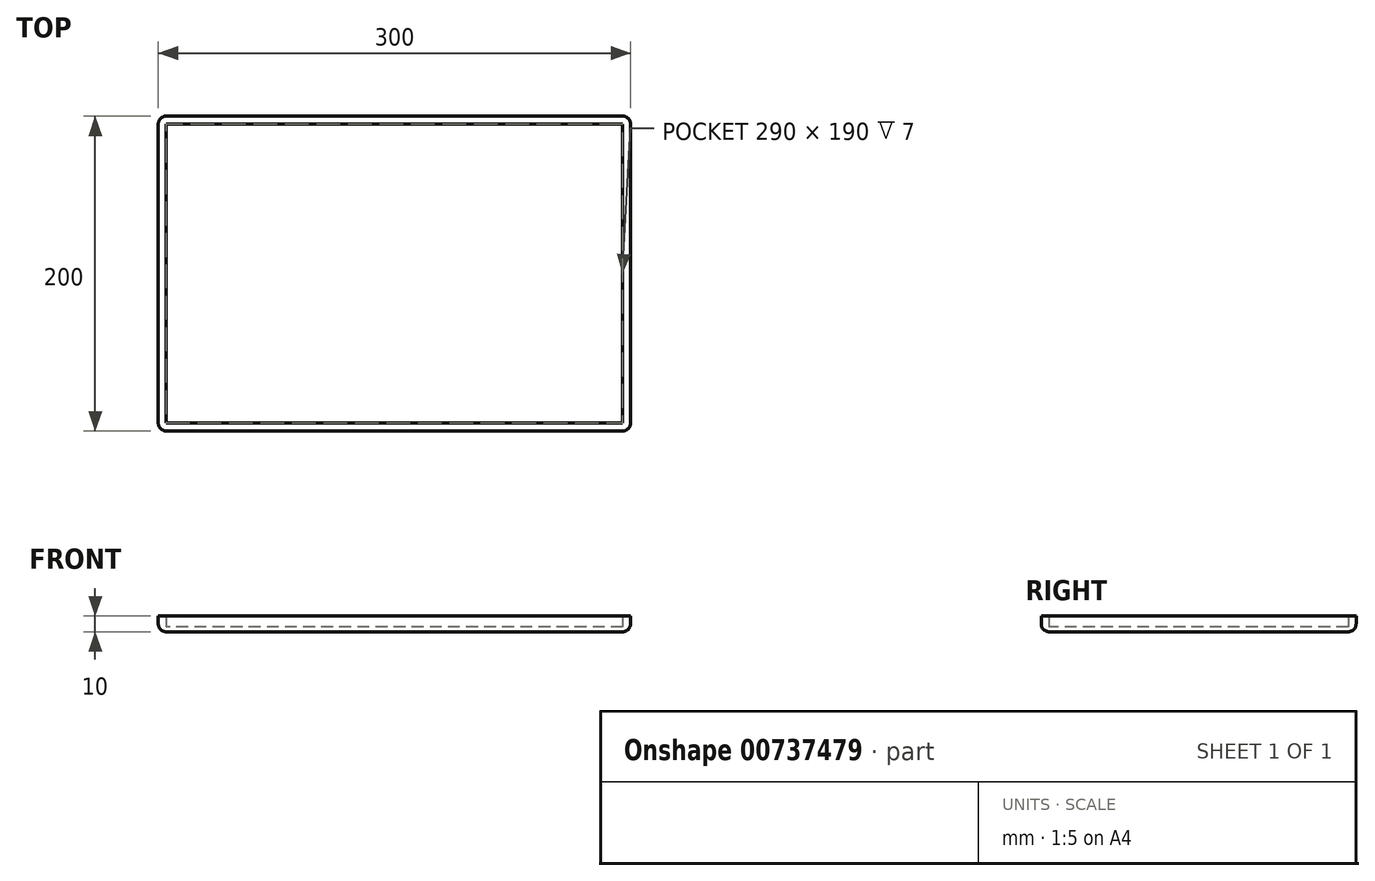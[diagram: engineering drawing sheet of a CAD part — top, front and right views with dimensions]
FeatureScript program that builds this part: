
annotation { "Feature Type Name" : "Feature", "Feature Type Description" : "" }
export const myFeature = defineFeature(function(context is Context, id is Id, definition is map)
    precondition{}
    {
        {
            var Q0;
            Q0=qCreatedBy(makeId("Top.planeOp"),FACE);
            var sketch = newSketch(context, id + "F0", { "sketchPlane" : qUnion([Q0])});
            skLineSegment(sketch, "E0.bottom", {"start": v(150, 100) * mm, "end": v(-150, 100) * mm});
            skLineSegment(sketch, "E0.top", {"start": v(150, -100) * mm, "end": v(-150, -100) * mm});
            skLineSegment(sketch, "E0.left", {"start": v(150, 100) * mm, "end": v(150, -100) * mm});
            skLineSegment(sketch, "E0.right", {"start": v(-150, 100) * mm, "end": v(-150, -100) * mm});
            skPoint(sketch, "E0.middle", {"position": v(0, 0) * mm});
            skLineSegment(sketch, "E1.bottom", {"start": v(145, 95) * mm, "end": v(-145, 95) * mm});
            skLineSegment(sketch, "E1.top", {"start": v(145, -95) * mm, "end": v(-145, -95) * mm});
            skLineSegment(sketch, "E1.left", {"start": v(145, 95) * mm, "end": v(145, -95) * mm});
            skLineSegment(sketch, "E1.right", {"start": v(-145, 95) * mm, "end": v(-145, -95) * mm});
            skLineSegment(sketch, "E2.bottom", {"start": v(147.5, 97.5) * mm, "end": v(-147.5, 97.5) * mm});
            skLineSegment(sketch, "E2.top", {"start": v(147.5, -97.5) * mm, "end": v(-147.5, -97.5) * mm});
            skLineSegment(sketch, "E2.left", {"start": v(147.5, 97.5) * mm, "end": v(147.5, -97.5) * mm});
            skLineSegment(sketch, "E2.right", {"start": v(-147.5, 97.5) * mm, "end": v(-147.5, -97.5) * mm});
            skSolve(sketch);
        }
        {
            var Q0;
            Q0=makeQuery(id+"F0.imprint","IMPRINT",FACE,{"disambiguationData":[TD([[makeQuery(id+"F0.imprint","IMPRINT",EDGE,{"derivedFrom":sQuery(id+"F0.wireOp",EDGE,"E0.bottom")}),1.0]])]});
            var Q1;
            Q1=makeQuery(id+"F0.imprint","IMPRINT",FACE,{"disambiguationData":[TD([[makeQuery(id+"F0.imprint","IMPRINT",EDGE,{"derivedFrom":sQuery(id+"F0.wireOp",EDGE,"E1.bottom")}),-1.0]])]});
            extrude(context, id + "F1", {"entities" : qUnion([Q0, Q1]), "depth" : 10 * mm, "offsetDistance" : 25 * mm});
        }
        {
            var Q0;
            Q0=makeQuery(id+"F0.imprint","IMPRINT",FACE,{"disambiguationData":[TD([[makeQuery(id+"F0.imprint","IMPRINT",EDGE,{"derivedFrom":sQuery(id+"F0.wireOp",EDGE,"E1.bottom")}),-1.0]])]});
            extrude(context, id + "F2", {"entities" : qUnion([Q0]), "operationType" : NewBodyOperationType.REMOVE, "depth" : 3 * mm, "offsetDistance" : 25 * mm});
        }
        {
            var Q0;
            Q0=makeQuery(id+"F0.imprint","IMPRINT",FACE,{"disambiguationData":[TD([[makeQuery(id+"F0.imprint","IMPRINT",EDGE,{"derivedFrom":sQuery(id+"F0.wireOp",EDGE,"E1.bottom")}),-1.0]])]});
            var Q1;
            Q1=makeQuery(id+"F0.imprint","IMPRINT",FACE,{"disambiguationData":[TD([[makeQuery(id+"F0.imprint","IMPRINT",EDGE,{"derivedFrom":sQuery(id+"F0.wireOp",EDGE,"E1.bottom")}),1.0]])]});
            extrude(context, id + "F3", {"entities" : qUnion([Q0, Q1]), "operationType" : NewBodyOperationType.ADD, "depth" : 3 * mm, "offsetDistance" : 25 * mm});
        }
        {
            var Q0;
            Q0=makeQuery(id+"F1.opExtrude","SWEPT_EDGE",EDGE,{"disambiguationData":[OSD([sQuery(id+"F0.wireOp",EDGE,"E0.top"),sQuery(id+"F0.wireOp",EDGE,"E0.right")])]});
            var Q1;
            Q1=makeQuery(id+"F1.opExtrude","SWEPT_EDGE",EDGE,{"disambiguationData":[OSD([sQuery(id+"F0.wireOp",EDGE,"E0.top"),sQuery(id+"F0.wireOp",EDGE,"E0.left")])]});
            var Q2;
            Q2=makeQuery(id+"F1.opExtrude","SWEPT_EDGE",EDGE,{"disambiguationData":[OSD([sQuery(id+"F0.wireOp",EDGE,"E0.bottom"),sQuery(id+"F0.wireOp",EDGE,"E0.left")])]});
            var Q3;
            Q3=makeQuery(id+"F1.opExtrude","SWEPT_EDGE",EDGE,{"disambiguationData":[OSD([sQuery(id+"F0.wireOp",EDGE,"E0.bottom"),sQuery(id+"F0.wireOp",EDGE,"E0.right")])]});
            fillet(context, id + "F4", {"entities" : qUnion([Q0, Q1, Q2, Q3]), "radius" : 5 * mm, "tangentPropagation" : true, "allowEdgeOverflow" : false});
        }
        {
            var Q0;
            Q0=makeQuery(id+"F3.boolean.opBoolean","MERGE",FACE,{"derivedFrom":[makeQuery(id+"F1.opExtrude","CAP_FACE",FACE,{"disambiguationData":[OSD([sQuery(id+"F0.wireOp",EDGE,"E0.bottom"),sQuery(id+"F0.wireOp",EDGE,"E0.top"),sQuery(id+"F0.wireOp",EDGE,"E0.left"),sQuery(id+"F0.wireOp",EDGE,"E0.right"),sQuery(id+"F0.wireOp",EDGE,"E1.bottom"),sQuery(id+"F0.wireOp",EDGE,"E1.top"),sQuery(id+"F0.wireOp",EDGE,"E1.left"),sQuery(id+"F0.wireOp",EDGE,"E1.right")])],"isStart":true}),makeQuery(id+"F3.opExtrude","CAP_FACE",FACE,{"disambiguationData":[OSD([sQuery(id+"F0.wireOp",EDGE,"E2.bottom"),sQuery(id+"F0.wireOp",EDGE,"E2.top"),sQuery(id+"F0.wireOp",EDGE,"E2.left"),sQuery(id+"F0.wireOp",EDGE,"E2.right")])],"isStart":true})]});
            fillet(context, id + "F5", {"entities" : qUnion([Q0]), "radius" : 5 * mm, "tangentPropagation" : true, "allowEdgeOverflow" : false});
        }
    });
